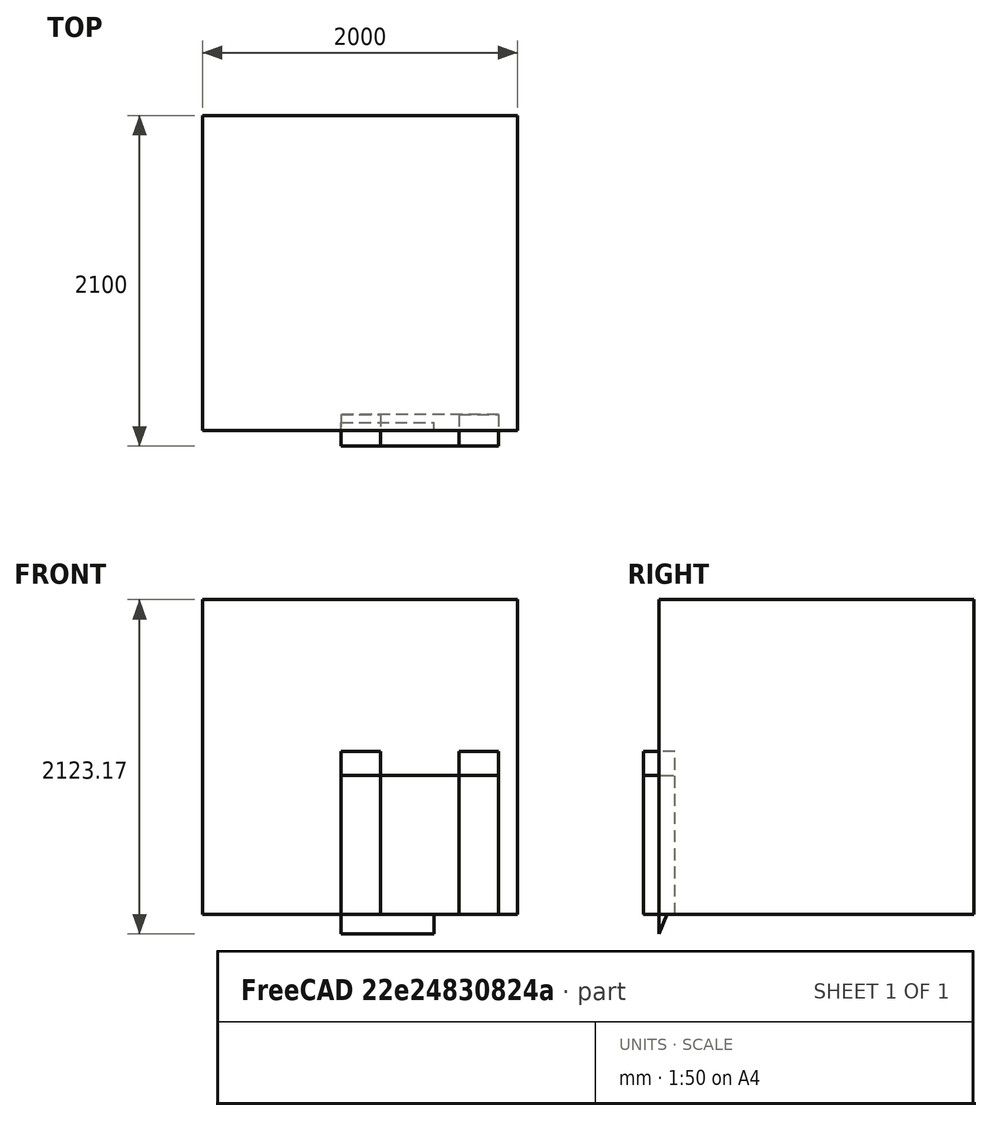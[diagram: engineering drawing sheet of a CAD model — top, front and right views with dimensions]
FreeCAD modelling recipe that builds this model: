
FCSTD DOCUMENT  (FreeCAD 0.21R33668 +26 (Git))
Label: intake-Edit3
License: Creative Commons Attribution-ShareAlike
LicenseURL: http://creativecommons.org/licenses/by-sa/4.0/
objects: Sketcher::SketchObject×12, PartDesign::Body×3, PartDesign::Plane×3, PartDesign::ShapeBinder×3, PartDesign::FeatureBase×2, Part::FeaturePython×2, Part::Cylinder×1, Part::Box×1, PartDesign::Boolean×1, PartDesign::Thickness×1, PartDesign::Hole×1, Part::Thickness×1, Mesh::Feature×1, PartDesign::Pad×1, App::Part×1
note: 35 computed .brp shape members not serialized (recipe doc carries the construction recipe); baked Part::Feature solids carry a one-line shape summary decoded from their .brp

FEATURE [Part::Cylinder] Cylinder
  Angle = 360
  AttacherType = Attacher::AttachEngine3D
  FirstAngle = 0
  Height = 915
  Placement = pos=(250,1004,0) rot=(-1,0,0;1.5708rad)
  Radius = 292.5
  SecondAngle = 0
  expr: .Placement.Rotation.Axis.x = 0 + 0
FEATURE [Part::Box] Box  label="Cube"
  AttacherType = Attacher::AttachEngine3D
  Height = 2000
  Length = 2000
  Placement = pos=(-450,0,0) rot=(0,0,1;0rad)
  Width = 2000
FEATURE [PartDesign::FeatureBase] BaseFeature
  BaseFeature = -> Cylinder
FEATURE [PartDesign::FeatureBase] BaseFeature001
  BaseFeature = -> Box
FEATURE [PartDesign::Body] Body001
  BaseFeature = -> Box
  Group = -> [BaseFeature001]
  Origin = -> Origin001
  Placement = pos=(-880,0,0) rot=(0,0,1;0rad)
  Tip = -> BaseFeature001
FEATURE [PartDesign::Boolean] Boolean
  BaseFeature = -> BaseFeature
  Group = -> [Box,Body001]
  Type = 1
FEATURE [Sketcher::SketchObject] Sketch003
  FullyConstrained = true
  MapMode = 2
  Placement = pos=(-880,0,0) rot=(0,0,1;0rad)
  Support = -> [Body001]
FEATURE [PartDesign::Thickness] Thickness
  Base = -> Boolean [Face2]
  BaseFeature = -> Boolean
  Intersection = false
  Join = 0
  Mode = 0
  Refine = true
  SupportTransform = false
  Value = 20
FEATURE [PartDesign::Plane] DatumPlane001
  Length = 716.856
  MapMode = 5
  Placement = pos=(0,0,915) rot=(1,0,0;3.14159rad)
  ResizeMode = 0
  Support = -> [Thickness]
  Width = 429.356
FEATURE [PartDesign::Hole] Hole
  BaseFeature = -> Thickness
  CustomThreadClearance = 0
  Depth = 25
  DepthType = 0
  Diameter = 4.8
  DrillForDepth = false
  DrillPoint = 1
  DrillPointAngle = 118
  HoleCutCountersinkAngle = 90
  HoleCutCustomValues = false
  HoleCutDepth = 0
  HoleCutDiameter = 6.1
  HoleCutType = 0
  ModelThread = false
  Profile = -> DatumPlane001
  Refine = true
  Tapered = false
  TaperedAngle = 90
  ThreadClass = 0
  ThreadDepth = 25
  ThreadDepthType = 0
  ThreadDirection = 0
  ThreadFit = 0
  ThreadSize = 0
  ThreadType = 5
  Threaded = true
  UseCustomThreadClearance = false
FEATURE [Sketcher::SketchObject] Sketch004
  FullyConstrained = true
  MapMode = 5
  Placement = pos=(0,0,1) rot=(0,0,1;0rad)
FEATURE [PartDesign::ShapeBinder] CopyWall
  TraceSupport = false
FEATURE [Sketcher::SketchObject] Sketch007
  FullyConstrained = true
  MapMode = 5
  Placement = pos=(0,-100,0) rot=(1,0,0;1.5708rad)
  Support = -> [CopyWall]
FEATURE [PartDesign::ShapeBinder] CopyWall001
  TraceSupport = false
FEATURE [Sketcher::SketchObject] Sketch009
  FullyConstrained = true
  MapMode = 5
  Placement = pos=(0,-100,0) rot=(1,0,0;1.5708rad)
  Support = -> [CopyWall001]
FEATURE [PartDesign::Plane] DatumPlane
  Length = 779.919
  MapMode = 5
  Placement = pos=(0,0,0) rot=(0,0.707107,0.707107;3.14159rad)
  ResizeMode = 0
  Support = -> [Hole]
  Width = 1114.92
FEATURE [Sketcher::SketchObject] Sketch  label="weir base sketch"
  FullyConstrained = true
  MapMode = 5
  Placement = pos=(0,0,935) rot=(0,0,1;0rad)
  Support = -> [DatumPlane]
  sketch-geometry (3):
    g0: LineSegment StartX=0 StartY=0 StartZ=0 EndX=250 EndY=0 EndZ=0
    g1: LineSegment StartX=250 StartY=0 StartZ=0 EndX=750 EndY=0 EndZ=0
    g2: LineSegment StartX=750 StartY=0 StartZ=0 EndX=1000 EndY=0 EndZ=0
  constraints (9):
    c: Coincident(g-1,g0)
    c: PointOnObject(g0,g-1)
    c: Coincident(g0,g1)
    c: PointOnObject(g1,g-1)
    c: Coincident(g1,g2)
    c: PointOnObject(g2,g-1)
    c: Distance(g0) = 250
    c: Distance(g1) = 500
    c: Distance(g2) = 250
FEATURE [Sketcher::SketchObject] Sketch001  label="weir notch bottom sketch"
  ExternalGeometry = -> [Sketch]
  FullyConstrained = true
  sketch-geometry (1):
    g0: LineSegment StartX=1000 StartY=0 StartZ=0 EndX=0 EndY=0 EndZ=0
  constraints (2):
    c: Coincident(g0,g-4)
    c: Coincident(g0,g-1)
FEATURE [Sketcher::SketchObject] Sketch002  label="weir notch top sketch"
  ExternalGeometry = -> [Sketch]
  FullyConstrained = true
  MapMode = 2
  Support = -> [Sketch001]
  sketch-geometry (2):
    g0: LineSegment StartX=0 StartY=0 StartZ=0 EndX=250 EndY=0 EndZ=0
    g1: LineSegment StartX=750 StartY=0 StartZ=0 EndX=1000 EndY=0 EndZ=0
  constraints (4):
    c: Coincident(g0,g-1)
    c: Coincident(g0,g-4)
    c: Coincident(g1,g-3)
    c: Coincident(g1,g-3)
FEATURE [Part::FeaturePython] Wall  label="weir (notch bottom)"  # Arch/BIM 166 (typed FeaturePython)
  Align = 2
  Area = 885000
  Base = -> Sketch001
  BlockHeight = 0
  BlockLength = 0
  CountBroken = 0
  CountEntire = 0
  Face = 0
  Height = 885
  HorizontalArea = 200000
  IfcData = attributes={"GlobalId": {"name": "GlobalId", "type": "IfcGloballyUniqueId", "is_enum": false, "enum_values": []}, "Description": {"... (+533 chars omitted),+1 more (map truncated)
  IfcType = 166
  Joint = 0
  Length = 1000
  MakeBlocks = false
  MoveBase = false
  MoveWithHost = false
  Normal = (0,0,0)
  OffsetFirst = 0
  OffsetSecond = 0
  PerimeterLength = 2400
  PredefinedType = 0
  VerticalArea = 2.124e+06
  Width = 200
  expr: Height = 300 mm + 585 mm
FEATURE [Part::FeaturePython] Wall001  label="weir (notch top)"  # Arch/BIM 166 (typed FeaturePython)
  Align = 2
  Area = 517500
  Base = -> Sketch002
  BlockHeight = 0
  BlockLength = 0
  CountBroken = 0
  CountEntire = 0
  Face = 0
  Height = 1035
  HorizontalArea = 100000
  IfcData = attributes={"GlobalId": {"name": "GlobalId", "type": "IfcGloballyUniqueId", "is_enum": false, "enum_values": []}, "Description": {"... (+533 chars omitted),+1 more (map truncated)
  IfcType = 166
  Joint = 0
  Length = 500
  MakeBlocks = false
  MoveBase = false
  MoveWithHost = false
  Normal = (0,0,0)
  OffsetFirst = 0
  OffsetSecond = 0
  PerimeterLength = 0
  PredefinedType = 0
  VerticalArea = 1.863e+06
  Width = 200
  expr: Height = 450 mm + 585 mm
FEATURE [Sketcher::SketchObject] Sketch005
  FullyConstrained = true
  MapMode = 2
  Support = -> [Wall]
FEATURE [PartDesign::Plane] DatumPlane002
  Length = 716.856
  MapMode = 5
  Placement = pos=(0,0,915) rot=(1,0,0;3.14159rad)
  ResizeMode = 0
  Support = -> [Hole,Sketch005]
  Width = 429.356
FEATURE [PartDesign::Body] Body  label="intake drum"
  BaseFeature = -> Cylinder
  Group = -> [BaseFeature,Boolean,Thickness,DatumPlane001,Hole,DatumPlane002,Sketch004,CopyWall,Sketch007,CopyWall001,Sketch009,DatumPlane]
  Origin = -> Origin
  Placement = pos=(500,1060,292.5) rot=(-1,0,0;4.97419rad)
  Tip = -> Hole
  expr: .Placement.Base.x = 500 mm / 2 + 250 mm
  expr: .Placement.Base.y = 915 mm + 100 mm + 45 mm
  expr: .Placement.Base.z = 585 mm / 2
FEATURE [Part::Thickness] Thickness001
  Faces = -> Body
  Intersection = false
  Join = 0
  Mode = 0
  SelfIntersection = false
  Value = 1
FEATURE [Sketcher::SketchObject] Sketch010
  FullyConstrained = false
  MapMode = 2
  Support = -> [XY_Plane003]
  sketch-geometry (4):
    g0: LineSegment StartX=157.218 StartY=1119.07 StartZ=0 EndX=857.218 EndY=1119.07 EndZ=0
    g1: LineSegment StartX=857.218 StartY=1119.07 StartZ=0 EndX=857.218 EndY=119.072 EndZ=0
    g2: LineSegment StartX=857.218 StartY=119.072 StartZ=0 EndX=157.218 EndY=119.072 EndZ=0
    g3: LineSegment StartX=157.218 StartY=119.072 StartZ=0 EndX=157.218 EndY=1119.07 EndZ=0
  constraints (10):
    c: Coincident(g0,g1)
    c: Coincident(g1,g2)
    c: Coincident(g2,g3)
    c: Coincident(g3,g0)
    c: Horizontal(g0)
    c: Horizontal(g2)
    c: Vertical(g1)
    c: Vertical(g3)
    c: DistanceX(g0,g0) = 700
    c: DistanceY(g3,g3) = 1000
FEATURE [PartDesign::ShapeBinder] ShapeBinder
  Placement = pos=(0,0,0) rot=(0,0.707107,0.707107;3.14159rad)
  Support = -> [DatumPlane]
  TraceSupport = false
FEATURE [Sketcher::SketchObject] Sketch011
  FullyConstrained = true
  MapMode = 5
  Placement = pos=(0,0,0) rot=(0,0.707107,0.707107;3.14159rad)
  Support = -> [ShapeBinder]
FEATURE [Mesh::Feature] expandedMetalMesh
  Placement = pos=(189.43,986.468,389.954) rot=(0.135504,0.137889,0.981135;4.6759rad)
FEATURE [Sketcher::SketchObject] Sketch012
  FullyConstrained = true
  MapMode = 5
  Placement = pos=(0,0,0) rot=(1,0,0;1.5708rad)
  Support = -> [XZ_Plane004]
FEATURE [Sketcher::SketchObject] Sketch013
  FullyConstrained = false
  MapMode = 5
  Placement = pos=(0,0,0) rot=(0.57735,0.57735,0.57735;2.0944rad)
  Support = -> [YZ_Plane003]
  sketch-geometry (3):
    g0: LineSegment StartX=0 StartY=0 StartZ=0 EndX=0 EndY=-123.169 EndZ=0
    g1: LineSegment StartX=0 StartY=-123.169 StartZ=0 EndX=49.4422 EndY=1.42e-14 EndZ=0
    g2: LineSegment StartX=49.4422 StartY=1.42e-14 StartZ=0 EndX=0 EndY=0 EndZ=0
  constraints (6):
    c: Coincident(g0,g-1)
    c: PointOnObject(g0,g-2)
    c: Coincident(g1,g0)
    c: PointOnObject(g1,g-1)
    c: Coincident(g2,g1)
    c: Coincident(g2,g0)
FEATURE [PartDesign::Pad] Pad
  Direction = (1,-2e-16,3e-16)
  Length = 590
  Length2 = 10
  Placement = pos=(205,115,645) rot=(1,1,1;2.0944rad)
  Profile = -> Sketch013
  ReferenceAxis = -> Sketch013 [N_Axis]
  Refine = true
  Type = 0
FEATURE [PartDesign::Body] Body002
  Group = -> [ShapeBinder,Sketch011,Sketch012,Sketch013,Pad]
  Origin = -> Origin004
  Tip = -> Pad
FEATURE [App::Part] Part001
  Group = -> [Body002]
  Origin = -> Origin003
